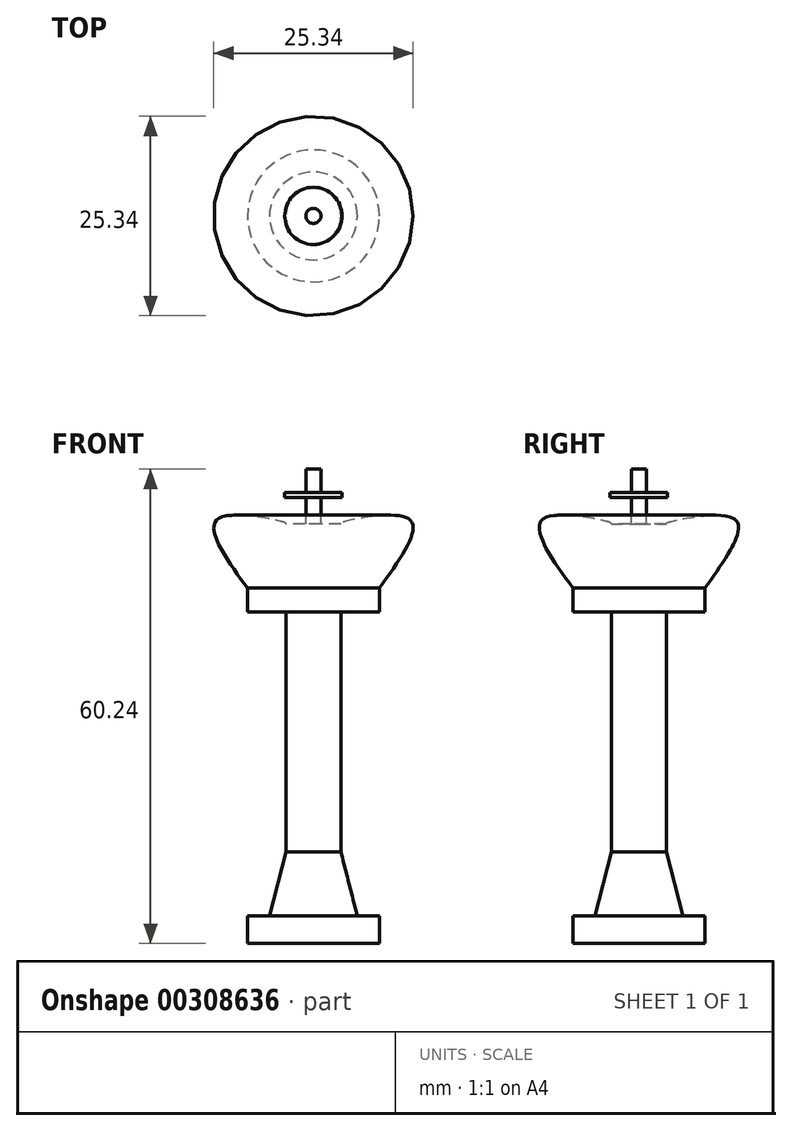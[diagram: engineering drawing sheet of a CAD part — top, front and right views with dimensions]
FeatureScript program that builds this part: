
annotation { "Feature Type Name" : "Feature", "Feature Type Description" : "" }
export const myFeature = defineFeature(function(context is Context, id is Id, definition is map)
    precondition{}
    {
        {
            var Q0;
            Q0=qCreatedBy(makeId("Front.planeOp"),FACE);
            var sketch = newSketch(context, id + "F0", { "sketchPlane" : qUnion([Q0])});
            skLineSegment(sketch, "E0", {"start": v(0, 23.96) * mm, "end": v(0, -36.28) * mm});
            skLineSegment(sketch, "E1", {"start": v(0, -36.28) * mm, "end": v(-8.37, -36.28) * mm});
            skLineSegment(sketch, "E2", {"start": v(-8.37, -36.28) * mm, "end": v(-8.37, -32.8) * mm});
            skLineSegment(sketch, "E3", {"start": v(-8.37, -32.8) * mm, "end": v(-5.58, -32.8) * mm});
            skLineSegment(sketch, "E4", {"start": v(-5.58, -32.8) * mm, "end": v(-3.49, -24.65) * mm});
            skLineSegment(sketch, "E5", {"start": v(-3.49, -24.65) * mm, "end": v(-3.49, 5.81) * mm});
            skLineSegment(sketch, "E6", {"start": v(-3.49, 5.81) * mm, "end": v(-8.37, 5.81) * mm});
            skLineSegment(sketch, "E7", {"start": v(-8.37, 5.81) * mm, "end": v(-8.37, 8.84) * mm});
            skFitSpline(sketch, "E8", {"points": [v(-8.37, 8.84) * mm, v(-12.1, 17.68) * mm, v(-3.72, 17.21) * mm, v(-3.49, 16.98) * mm], "startDerivative": vector(-17.57, 24.24) * mm, "endDerivative": vector(0, -5.1) * mm});
            skLineSegment(sketch, "E9", {"start": v(-3.49, 16.98) * mm, "end": v(-0.96, 16.98) * mm});
            skLineSegment(sketch, "E10", {"start": v(-0.96, 16.98) * mm, "end": v(-0.96, 20.38) * mm});
            skLineSegment(sketch, "E11", {"start": v(-0.96, 20.38) * mm, "end": v(-3.64, 20.38) * mm});
            skLineSegment(sketch, "E12", {"start": v(-3.64, 20.38) * mm, "end": v(-3.64, 21) * mm});
            skLineSegment(sketch, "E13", {"start": v(-3.64, 21) * mm, "end": v(-0.96, 21) * mm});
            skLineSegment(sketch, "E14", {"start": v(-0.96, 21) * mm, "end": v(-0.96, 23.96) * mm});
            skLineSegment(sketch, "E15", {"start": v(-0.96, 23.96) * mm, "end": v(0, 23.96) * mm});
            skSolve(sketch);
        }
        {
            var Q0;
            Q0 = qSketchRegion(id + "F0", true);
            var Q1;
            Q1=sQuery(id+"F0.wireOp",EDGE,"E0");
            revolve(context, id + "F1", {"entities" : qUnion([Q0]), "axis" : qUnion([Q1]), "revolveType" : RevolveType.FULL});
        }
    });
